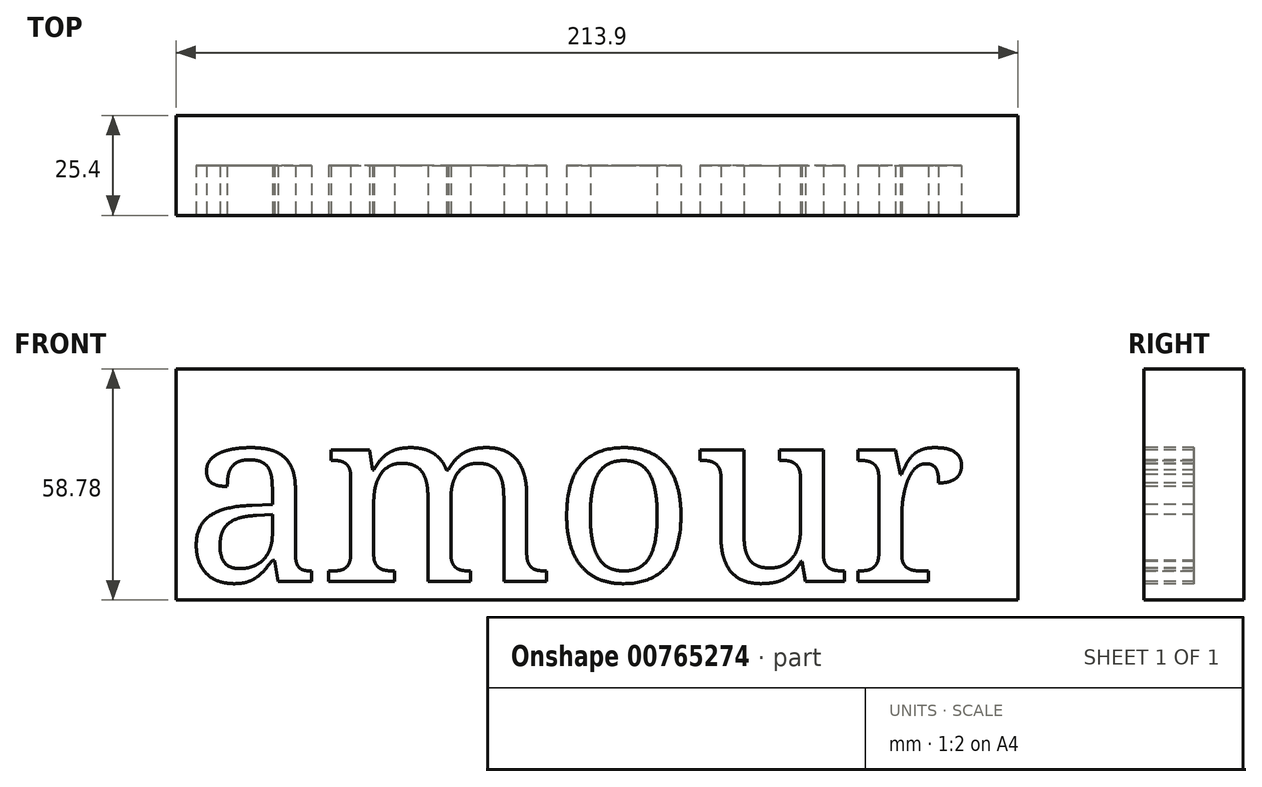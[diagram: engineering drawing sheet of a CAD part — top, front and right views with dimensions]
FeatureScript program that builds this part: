
annotation { "Feature Type Name" : "Feature", "Feature Type Description" : "" }
export const myFeature = defineFeature(function(context is Context, id is Id, definition is map)
    precondition{}
    {
        {
            var Q0;
            Q0=qCreatedBy(makeId("Front.planeOp"),FACE);
            var sketch = newSketch(context, id + "F0", { "sketchPlane" : qUnion([Q0])});
            skLineSegment(sketch, "E0.bottom", {"start": v(106.95, -29.39) * mm, "end": v(-106.95, -29.39) * mm});
            skLineSegment(sketch, "E0.top", {"start": v(106.95, 29.39) * mm, "end": v(-106.95, 29.39) * mm});
            skLineSegment(sketch, "E0.left", {"start": v(106.95, -29.39) * mm, "end": v(106.95, 29.39) * mm});
            skLineSegment(sketch, "E0.right", {"start": v(-106.95, -29.39) * mm, "end": v(-106.95, 29.39) * mm});
            skPoint(sketch, "E0.middle", {"position": v(0, 0) * mm});
            skSolve(sketch);
        }
        {
            var Q0;
            Q0 = qSketchRegion(id + "F0", true);
            extrude(context, id + "F1", {"entities" : qUnion([Q0]), "depth" : 25.4 * mm, "offsetDistance" : 25.4 * mm});
        }
        {
            var Q0;
            Q0=makeQuery(id+"F1.opExtrude","CAP_FACE",FACE,{"disambiguationData":[OSD([sQuery(id+"F0.wireOp",EDGE,"E0.bottom"),sQuery(id+"F0.wireOp",EDGE,"E0.top"),sQuery(id+"F0.wireOp",EDGE,"E0.left"),sQuery(id+"F0.wireOp",EDGE,"E0.right")])],"isStart":false});
            var sketch = newSketch(context, id + "F2", { "sketchPlane" : qUnion([Q0])});
            skText(sketch, "E1", { "text": "amour", "fontName": "NotoSerif-Regular.ttf"});
            const initialGuessF2  = {"E1": [-0.10495, -0.02459, 1, 0, 0.04478]};
            skSetInitialGuess(sketch, initialGuessF2);
            skSolve(sketch);
        }
        {
            var Q0;
            Q0 = qSketchRegion(id + "F2", true);
            extrude(context, id + "F3", {"entities" : qUnion([Q0]), "operationType" : NewBodyOperationType.REMOVE, "depth" : -12.7 * mm, "offsetDistance" : 25.4 * mm});
        }
    });
